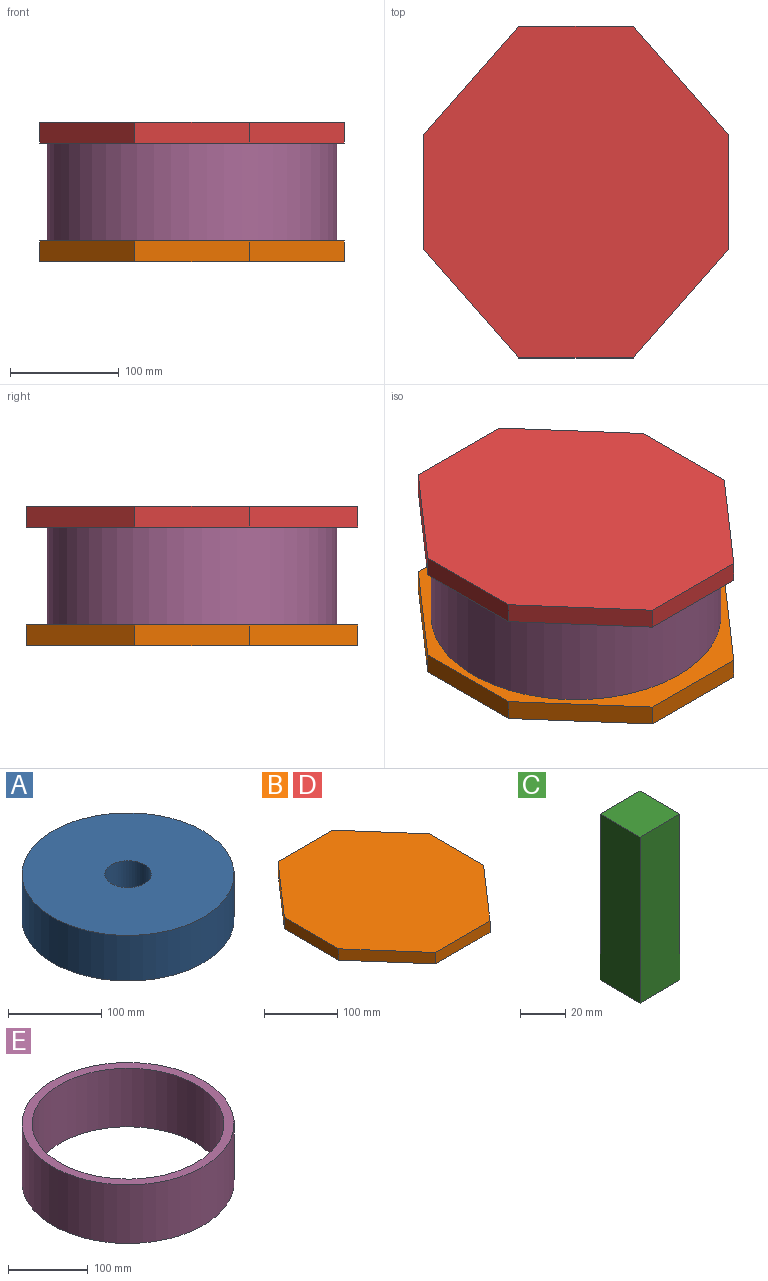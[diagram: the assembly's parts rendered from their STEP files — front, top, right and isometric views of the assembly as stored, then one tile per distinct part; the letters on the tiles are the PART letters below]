
ASSEMBLY  parts=5 mates=7
PART A: 4 faces, bbox 228x228x60 mm
  f0: cylinder r=25mm len=60mm, axis (0,0,-1), area 9424.8mm2, adj f2,f3
  f1: cylinder r=114mm len=228mm, axis (0,0,-1), area 42977mm2, adj f2,f3
  f2: plane 228x228mm, normal (0,0,1), area 38864.6mm2, adj f0,f1
  f3: plane 228x228mm, normal (0,0,-1), area 38864.6mm2, adj f0,f1
PART B: 10 faces, bbox 280x304.8x19 mm
  f0: plane 105.27x19mm, normal (1,0,0), area 2000.1mm2, adj f4,f5,f7,f8
  f1: plane 105.27x19mm, normal (0,1,0), area 2000.1mm2, adj f4,f5,f6,f7
  f2: plane 105.27x19mm, normal (-1,0,0), area 2000.1mm2, adj f4,f5,f6,f9
  f3: plane 105.27x19mm, normal (0,-1,0), area 2000.1mm2, adj f4,f5,f8,f9
  f4: plane 304.8x280mm, normal (0,0,1), area 67912mm2, adj f0,f1,f2,f3,f6,f7,f8,f9
  f5: plane 304.8x280mm, normal (0,0,-1), area 67912mm2, adj f0,f1,f2,f3,f6,f7,f8,f9
  f6: plane 99.77x87.37mm, normal (-0.75,0.66,0), area 2519.6mm2, adj f1,f2,f4,f5
  f7: plane 99.77x87.37mm, normal (0.75,0.66,0), area 2519.6mm2, adj f0,f1,f4,f5
  f8: plane 99.77x87.37mm, normal (0.75,-0.66,0), area 2519.6mm2, adj f0,f3,f4,f5
  f9: plane 99.77x87.37mm, normal (-0.75,-0.66,0), area 2519.6mm2, adj f2,f3,f4,f5
PART C: 6 faces, bbox 25x25x90 mm
  f0: plane 90x25mm, normal (0,-1,0), area 2250mm2, adj f1,f3,f4,f5
  f1: plane 90x25mm, normal (1,0,0), area 2250mm2, adj f0,f2,f4,f5
  f2: plane 90x25mm, normal (0,1,0), area 2250mm2, adj f1,f3,f4,f5
  f3: plane 90x25mm, normal (-1,0,0), area 2250mm2, adj f0,f2,f4,f5
  f4: plane 25x25mm, normal (0,0,1), area 625mm2, adj f0,f1,f2,f3
  f5: plane 25x25mm, normal (0,0,-1), area 625mm2, adj f0,f1,f2,f3
PART D: same geometry as B
PART E: 4 faces, bbox 266.4x266.4x90 mm
  f0: cylinder r=120.5mm len=241mm, axis (0,0,-1), area 68141.1mm2, adj f2,f3
  f1: cylinder r=133.2mm len=266.4mm, axis (0,0,-1), area 75322.8mm2, adj f2,f3
  f2: plane 266.4x266.4mm, normal (0,0,1), area 10122.2mm2, adj f0,f1
  f3: plane 266.4x266.4mm, normal (0,0,-1), area 10122.2mm2, adj f0,f1
PLACE A t=(0,0,44)mm
PLACE B at identity fixed
PLACE C rot(axis=(0,0,1),0deg) t=(0,0,19)mm
PLACE D t=(0,0,109)mm
PLACE E rot(axis=(0,0,-1),13.6deg) t=(0,0,19)mm
MATE planar E.f1 <-> B.f4  axis (0,0,-1) through (0,0,19)mm
MATE cylindrical E.f0 <-> D.f5  axis (0,0,-1) through (0,0,64)mm
MATE fastened C.f4 <-> D.f5  axis (0,0,1) through (0,0,109)mm
MATE fastened B.f4 <-> C.f5  axis (0,0,1) through (0,0,19)mm
MATE cylindrical A.f1 <-> E.f1  axis (0,0,-1) through (0,0,74)mm
MATE cylindrical E.f0 <-> B.f4  axis (0,0,-1) through (0,0,64)mm
MATE cylindrical C.f5 <-> B.f4  axis (0,0,-1) through (0,0,19)mm
